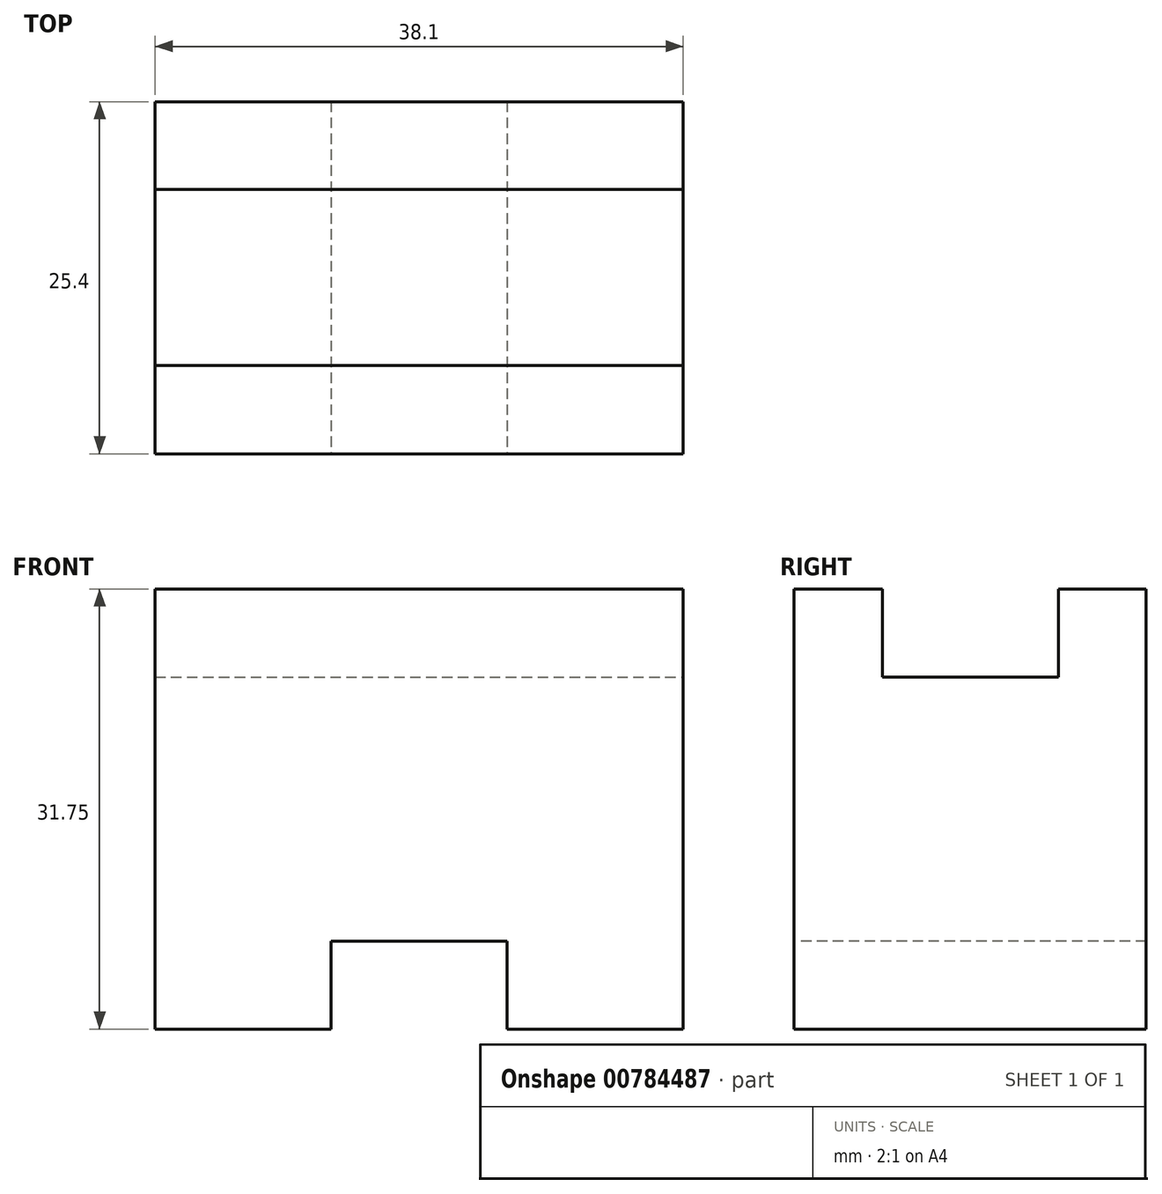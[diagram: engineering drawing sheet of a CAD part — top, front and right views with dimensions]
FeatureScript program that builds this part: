
annotation { "Feature Type Name" : "Feature", "Feature Type Description" : "" }
export const myFeature = defineFeature(function(context is Context, id is Id, definition is map)
    precondition{}
    {
        {
            var Q0;
            Q0=qCreatedBy(makeId("Front.planeOp"),FACE);
            var sketch = newSketch(context, id + "F0", { "sketchPlane" : qUnion([Q0])});
            skLineSegment(sketch, "E0", {"start": v(0, 0) * mm, "end": v(38.1, 0) * mm});
            skLineSegment(sketch, "E1", {"start": v(38.1, 0) * mm, "end": v(38.1, 31.75) * mm});
            skLineSegment(sketch, "E2", {"start": v(38.1, 31.75) * mm, "end": v(0, 31.75) * mm});
            skLineSegment(sketch, "E3", {"start": v(0, 31.75) * mm, "end": v(0, 0) * mm});
            skSolve(sketch);
        }
        {
            var Q0;
            Q0 = qSketchRegion(id + "F0", true);
            extrude(context, id + "F1", {"entities" : qUnion([Q0]), "depth" : 25.4 * mm, "offsetDistance" : 25.4 * mm});
        }
        {
            var Q0;
            Q0=makeQuery(id+"F1.opExtrude","CAP_FACE",FACE,{"disambiguationData":[OSD([sQuery(id+"F0.wireOp",EDGE,"E0"),sQuery(id+"F0.wireOp",EDGE,"E1"),sQuery(id+"F0.wireOp",EDGE,"E2"),sQuery(id+"F0.wireOp",EDGE,"E3")])],"isStart":false});
            var sketch = newSketch(context, id + "F2", { "sketchPlane" : qUnion([Q0])});
            skLineSegment(sketch, "E4", {"start": v(0, 0) * mm, "end": v(12.7, 0) * mm});
            skLineSegment(sketch, "E5", {"start": v(12.7, 0) * mm, "end": v(12.7, 6.35) * mm});
            skLineSegment(sketch, "E6", {"start": v(12.7, 6.35) * mm, "end": v(25.4, 6.35) * mm});
            skLineSegment(sketch, "E7", {"start": v(25.4, 6.35) * mm, "end": v(25.4, 0) * mm});
            skSolve(sketch);
        }
        {
            var Q0;
            {var subQ0=sQuery(id+"F2.wireOp",EDGE,"E5");Q0=makeQuery(id+"F2.imprint","IMPRINT",FACE,{"disambiguationData":[TD([[makeQuery(id+"F2.imprint","IMPRINT",EDGE,{"derivedFrom":subQ0}),-1.0]])]});}
            extrude(context, id + "F3", {"entities" : qUnion([Q0]), "operationType" : NewBodyOperationType.REMOVE, "oppositeDirection" : true, "depth" : 25.4 * mm, "offsetDistance" : 25.4 * mm});
        }
        {
            var Q0;
            Q0=makeQuery(id+"F1.opExtrude","SWEPT_FACE",FACE,{"disambiguationData":[OSD([sQuery(id+"F0.wireOp",EDGE,"E1")])]});
            var sketch = newSketch(context, id + "F4", { "sketchPlane" : qUnion([Q0])});
            skLineSegment(sketch, "E8", {"start": v(-25.4, 31.75) * mm, "end": v(-19.04, 31.75) * mm});
            skLineSegment(sketch, "E9", {"start": v(-19.04, 31.75) * mm, "end": v(-19.04, 25.4) * mm});
            skLineSegment(sketch, "E10", {"start": v(-19.04, 25.4) * mm, "end": v(-6.34, 25.4) * mm});
            skLineSegment(sketch, "E11", {"start": v(-6.34, 25.4) * mm, "end": v(-6.34, 31.75) * mm});
            skSolve(sketch);
        }
        {
            var Q0;
            {var subQ0=sQuery(id+"F4.wireOp",EDGE,"E9");Q0=makeQuery(id+"F4.imprint","IMPRINT",FACE,{"disambiguationData":[TD([[makeQuery(id+"F4.imprint","IMPRINT",EDGE,{"derivedFrom":subQ0}),1.0]])]});}
            extrude(context, id + "F5", {"entities" : qUnion([Q0]), "operationType" : NewBodyOperationType.REMOVE, "oppositeDirection" : true, "depth" : 38.1 * mm, "offsetDistance" : 25.4 * mm});
        }
    });
